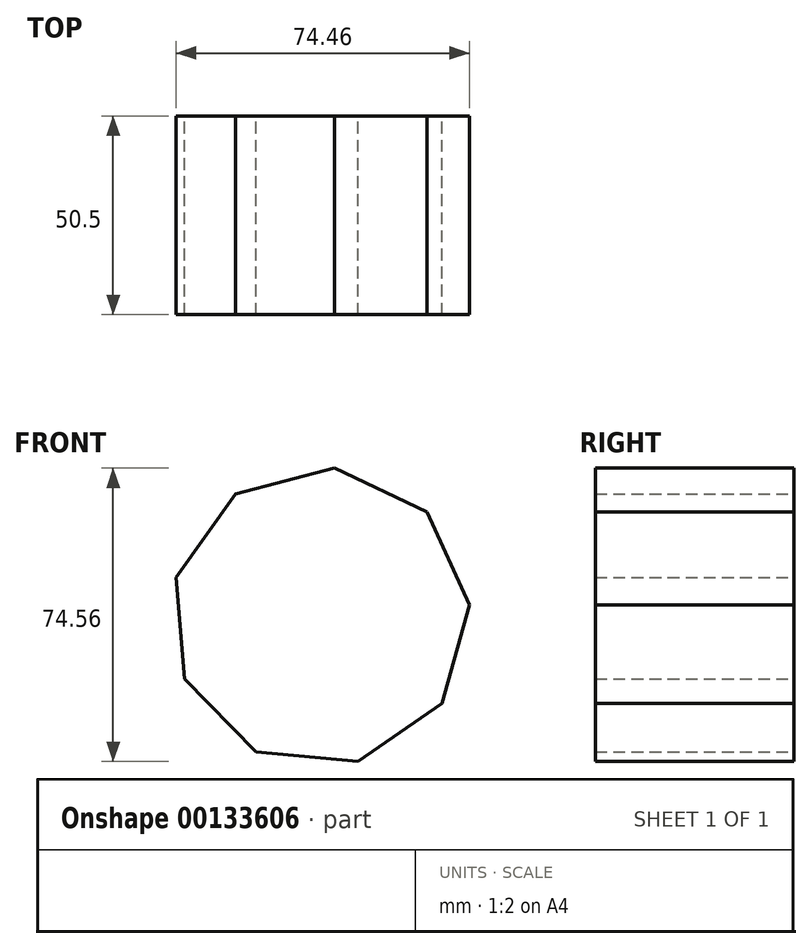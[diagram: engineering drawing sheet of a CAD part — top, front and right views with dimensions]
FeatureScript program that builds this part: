
annotation { "Feature Type Name" : "Feature", "Feature Type Description" : "" }
export const myFeature = defineFeature(function(context is Context, id is Id, definition is map)
    precondition{}
    {
        {
            var Q0;
            Q0=qCreatedBy(makeId("Front.planeOp"),FACE);
            var sketch = newSketch(context, id + "F0", { "sketchPlane" : qUnion([Q0])});
            skCircle(sketch, "E0.cCircle", {"center": v(-22.83, 29.38) * mm, "radius": 35.69 * mm, "construction": true});
            skLineSegment(sketch, "E0.0", {"start": v(8.11, 7.37) * mm, "end": v(-13.28, -7.37) * mm});
            skLineSegment(sketch, "E0.1", {"start": v(-13.28, -7.37) * mm, "end": v(-39.14, -4.91) * mm});
            skLineSegment(sketch, "E0.2", {"start": v(-39.14, -4.91) * mm, "end": v(-57.37, 13.6) * mm});
            skLineSegment(sketch, "E0.3", {"start": v(-57.37, 13.6) * mm, "end": v(-59.44, 39.48) * mm});
            skLineSegment(sketch, "E0.4", {"start": v(-59.44, 39.48) * mm, "end": v(-44.38, 60.65) * mm});
            skLineSegment(sketch, "E0.5", {"start": v(-44.38, 60.65) * mm, "end": v(-19.24, 67.19) * mm});
            skLineSegment(sketch, "E0.6", {"start": v(-19.24, 67.19) * mm, "end": v(4.22, 56.04) * mm});
            skLineSegment(sketch, "E0.7", {"start": v(4.22, 56.04) * mm, "end": v(15.02, 32.41) * mm});
            skLineSegment(sketch, "E0.8", {"start": v(15.02, 32.41) * mm, "end": v(8.11, 7.37) * mm});
            skPoint(sketch, "E0.0.midPoint", {"position": v(-2.58, 0) * mm});
            skSolve(sketch);
        }
        {
            var Q0;
            Q0=makeQuery(id+"F0.imprint","IMPRINT",FACE,{"disambiguationData":[TD([[makeQuery(id+"F0.imprint","IMPRINT",EDGE,{"derivedFrom":sQuery(id+"F0.wireOp",EDGE,"E0.0")}),-1.0]])]});
            extrude(context, id + "F1", {"entities" : qUnion([Q0]), "depth" : 50.5 * mm});
        }
    });
